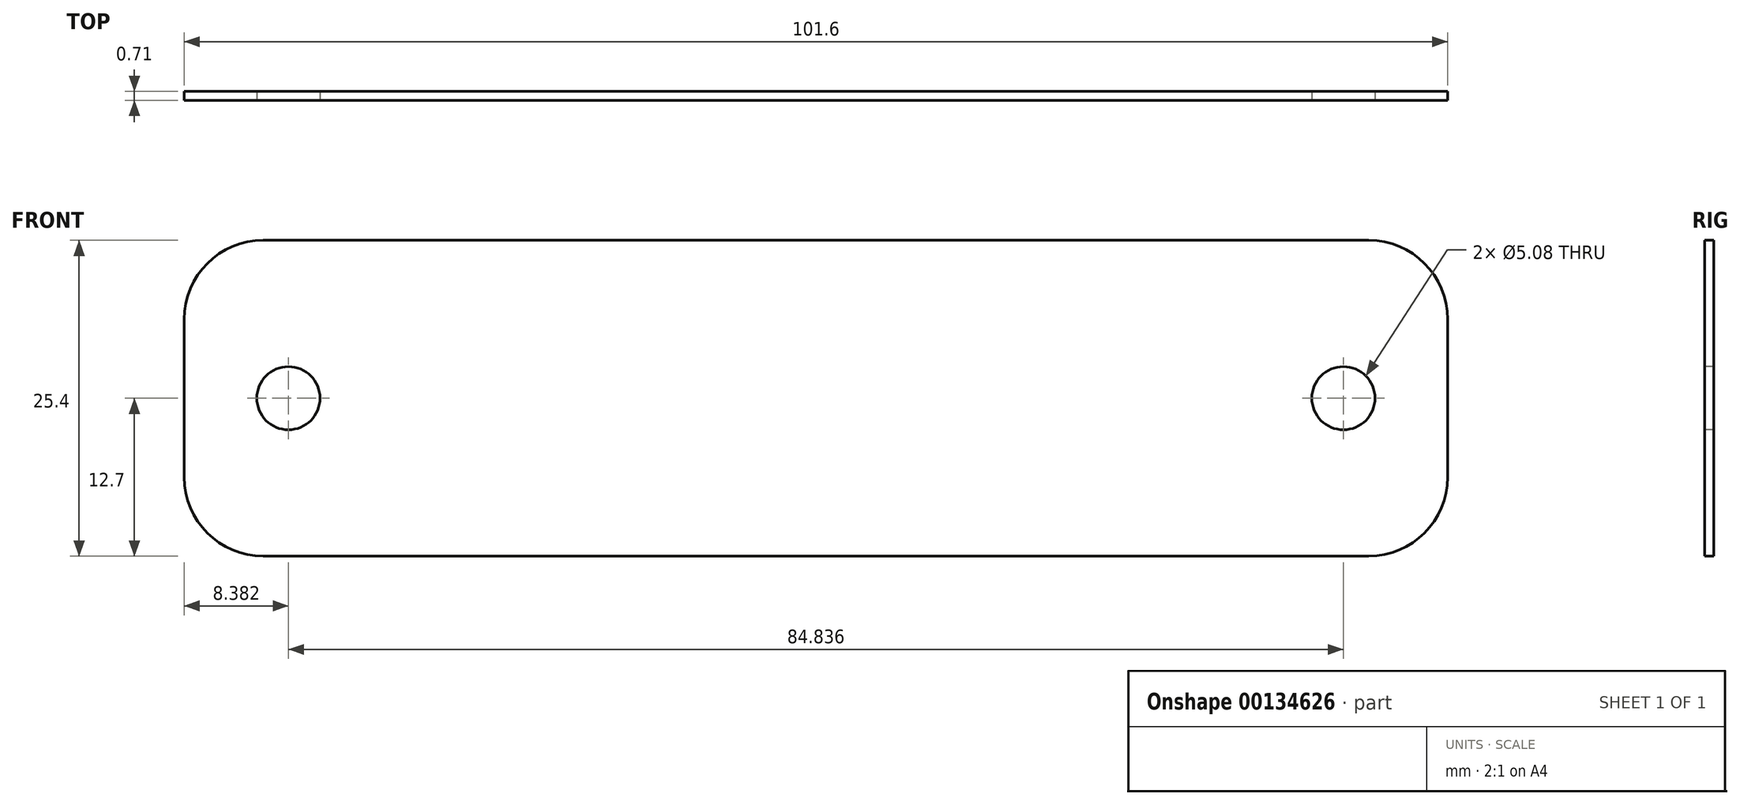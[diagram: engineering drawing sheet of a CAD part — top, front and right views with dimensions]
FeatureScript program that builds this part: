
annotation { "Feature Type Name" : "Feature", "Feature Type Description" : "" }
export const myFeature = defineFeature(function(context is Context, id is Id, definition is map)
    precondition{}
    {
        {
            var Q0;
            Q0=qCreatedBy(makeId("Front.planeOp"),FACE);
            var sketch = newSketch(context, id + "F0", { "sketchPlane" : qUnion([Q0])});
            skLineSegment(sketch, "E0", {"start": v(-40.8, 29.95) * mm, "end": v(48.1, 29.95) * mm});
            skLineSegment(sketch, "E1", {"start": v(-47.14, 23.6) * mm, "end": v(-47.14, 10.9) * mm});
            skLineSegment(sketch, "E2", {"start": v(-40.8, 4.55) * mm, "end": v(48.1, 4.55) * mm});
            skLineSegment(sketch, "E3", {"start": v(54.46, 10.9) * mm, "end": v(54.46, 23.6) * mm});
            skPoint(sketch, "E4.visualSharp", {"position": v(-47.14, 29.95) * mm});
            skArc(sketch, "E4.filletArc", {"start": v(-40.8, 29.95) * mm, "mid": v(-45.28, 28.1) * mm, "end": v(-47.14, 23.6) * mm});
            skPoint(sketch, "E5.visualSharp", {"position": v(-47.14, 4.55) * mm});
            skArc(sketch, "E5.filletArc", {"start": v(-47.14, 10.9) * mm, "mid": v(-45.28, 6.41) * mm, "end": v(-40.8, 4.55) * mm});
            skPoint(sketch, "E6.visualSharp", {"position": v(54.46, 29.95) * mm});
            skArc(sketch, "E6.filletArc", {"start": v(54.46, 23.6) * mm, "mid": v(52.6, 28.1) * mm, "end": v(48.1, 29.95) * mm});
            skPoint(sketch, "E7.visualSharp", {"position": v(54.46, 4.55) * mm});
            skArc(sketch, "E7.filletArc", {"start": v(48.1, 4.55) * mm, "mid": v(52.6, 6.41) * mm, "end": v(54.46, 10.9) * mm});
            skSolve(sketch);
        }
        {
            var Q0;
            Q0=makeQuery(id+"F0.imprint","IMPRINT",FACE,{"disambiguationData":[TD([[makeQuery(id+"F0.imprint","IMPRINT",EDGE,{"derivedFrom":sQuery(id+"F0.wireOp",EDGE,"E0")}),-1.0]])]});
            extrude(context, id + "F1", {"entities" : qUnion([Q0]), "depth" : 0.71 * mm});
        }
        {
            var Q0;
            Q0=makeQuery(id+"F1.opExtrude","CAP_FACE",FACE,{"disambiguationData":[OSD([sQuery(id+"F0.wireOp",EDGE,"E0"),sQuery(id+"F0.wireOp",EDGE,"E1"),sQuery(id+"F0.wireOp",EDGE,"E2"),sQuery(id+"F0.wireOp",EDGE,"E3"),sQuery(id+"F0.wireOp",EDGE,"E4.filletArc"),sQuery(id+"F0.wireOp",EDGE,"E5.filletArc"),sQuery(id+"F0.wireOp",EDGE,"E6.filletArc"),sQuery(id+"F0.wireOp",EDGE,"E7.filletArc")])],"isStart":false});
            var sketch = newSketch(context, id + "F2", { "sketchPlane" : qUnion([Q0])});
            skLineSegment(sketch, "E8", {"start": v(-47.14, 17.25) * mm, "end": v(-38.76, 17.25) * mm});
            skLineSegment(sketch, "E9", {"start": v(54.46, 17.25) * mm, "end": v(46.08, 17.25) * mm});
            skCircle(sketch, "E10", {"center": v(-38.76, 17.25) * mm, "radius": 2.54 * mm});
            skCircle(sketch, "E11", {"center": v(46.08, 17.25) * mm, "radius": 2.54 * mm});
            skSolve(sketch);
        }
        {
            var Q0;
            Q0=makeQuery(id+"F2.imprint","IMPRINT",FACE,{"disambiguationData":[TD([[makeQuery(id+"F2.imprint","IMPRINT",EDGE,{"derivedFrom":sQuery(id+"F2.wireOp",EDGE,"E10")}),1.0]])]});
            var Q1;
            Q1=makeQuery(id+"F2.imprint","IMPRINT",FACE,{"disambiguationData":[TD([[makeQuery(id+"F2.imprint","IMPRINT",EDGE,{"derivedFrom":sQuery(id+"F2.wireOp",EDGE,"E11")}),1.0]])]});
            extrude(context, id + "F3", {"entities" : qUnion([Q0, Q1]), "operationType" : NewBodyOperationType.REMOVE, "oppositeDirection" : true, "depth" : 25.4 * mm});
        }
    });
